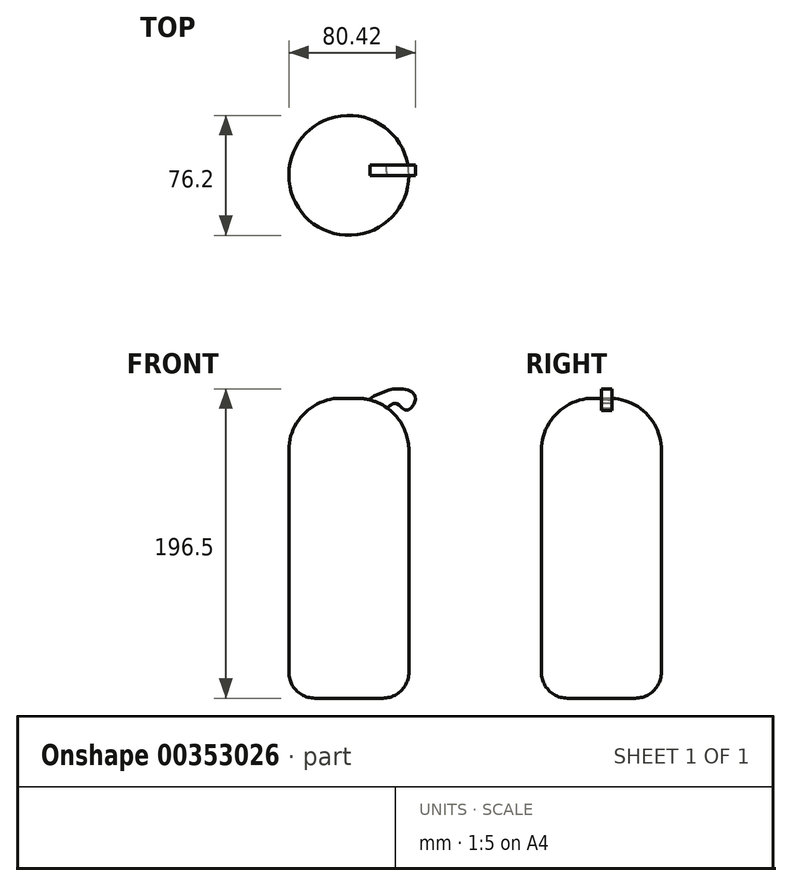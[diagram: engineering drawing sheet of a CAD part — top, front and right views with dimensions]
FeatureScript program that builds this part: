
annotation { "Feature Type Name" : "Feature", "Feature Type Description" : "" }
export const myFeature = defineFeature(function(context is Context, id is Id, definition is map)
    precondition{}
    {
        {
            var Q0;
            Q0=qCreatedBy(makeId("Front.planeOp"),FACE);
            var sketch = newSketch(context, id + "F0", { "sketchPlane" : qUnion([Q0])});
            skLineSegment(sketch, "E0.bottom", {"start": v(-0.42, 101.08) * mm, "end": v(9.74, 101.08) * mm});
            skLineSegment(sketch, "E0.top", {"start": v(-16.93, -89.42) * mm, "end": v(26.25, -89.42) * mm});
            skLineSegment(sketch, "E0.left", {"start": v(-33.44, 68.06) * mm, "end": v(-33.44, -72.91) * mm});
            skLineSegment(sketch, "E0.right", {"start": v(42.76, 68.06) * mm, "end": v(42.76, -72.91) * mm});
            skPoint(sketch, "E1.visualSharp", {"position": v(-33.44, 101.08) * mm});
            skArc(sketch, "E1.filletArc", {"start": v(-0.42, 101.08) * mm, "mid": v(-23.77, 91.4) * mm, "end": v(-33.44, 68.06) * mm});
            skPoint(sketch, "E2.visualSharp", {"position": v(42.76, 101.08) * mm});
            skArc(sketch, "E2.filletArc", {"start": v(42.76, 68.06) * mm, "mid": v(33.1, 91.4) * mm, "end": v(9.74, 101.08) * mm});
            skPoint(sketch, "E3.visualSharp", {"position": v(42.76, -89.42) * mm});
            skArc(sketch, "E3.filletArc", {"start": v(26.25, -89.42) * mm, "mid": v(37.93, -84.58) * mm, "end": v(42.76, -72.91) * mm});
            skPoint(sketch, "E4.visualSharp", {"position": v(-33.44, -89.42) * mm});
            skArc(sketch, "E4.filletArc", {"start": v(-33.44, -72.91) * mm, "mid": v(-28.6, -84.58) * mm, "end": v(-16.93, -89.42) * mm});
            skLineSegment(sketch, "E5", {"start": v(4.66, 101.08) * mm, "end": v(4.66, -89.42) * mm});
            skLineSegment(sketch, "E6", {"start": v(-30.48, 15.24) * mm, "end": v(-30.48, 0) * mm});
            skLineSegment(sketch, "E7", {"start": v(-15.24, 15.24) * mm, "end": v(-15.24, 0) * mm});
            skLineSegment(sketch, "E8", {"start": v(0, 15.24) * mm, "end": v(0, 0) * mm});
            skLineSegment(sketch, "E9", {"start": v(15.24, 15.24) * mm, "end": v(15.24, 0) * mm});
            skLineSegment(sketch, "E10", {"start": v(30.48, 15.24) * mm, "end": v(30.48, 0) * mm});
            skLineSegment(sketch, "E11", {"start": v(40.64, 15.24) * mm, "end": v(40.64, 0) * mm});
            skSolve(sketch);
        }
        {
            var Q0;
            Q0=makeQuery(id+"F0.imprint","IMPRINT",FACE,{"disambiguationData":[TD([[makeQuery(id+"F0.imprint","IMPRINT",EDGE,{"derivedFrom":sQuery(id+"F0.wireOp",EDGE,"E0.right")}),-1.0]])]});
            var Q1;
            Q1=sQuery(id+"F0.wireOp",EDGE,"E11");
            var Q2;
            Q2=sQuery(id+"F0.wireOp",EDGE,"E10");
            var Q3;
            Q3=sQuery(id+"F0.wireOp",EDGE,"E9");
            var Q4;
            Q4=sQuery(id+"F0.wireOp",EDGE,"E5");
            revolve(context, id + "F1", {"entities" : qUnion([Q0]), "surfaceEntities" : qUnion([Q1, Q2, Q3]), "axis" : qUnion([Q4]), "revolveType" : RevolveType.FULL});
        }
        {
            var Q0;
            Q0=qCreatedBy(makeId("Right.planeOp"),FACE);
            var sketch = newSketch(context, id + "F2", { "sketchPlane" : qUnion([Q0])});
            skLineSegment(sketch, "E12", {"start": v(37.35, 0) * mm, "end": v(37.35, 25.6) * mm});
            skLineSegment(sketch, "E13", {"start": v(-38.8, 0) * mm, "end": v(-38.8, 25.6) * mm});
            skSolve(sketch);
        }
        {
            var Q0;
            Q0 = qSketchRegion(id + "F2", true);
            var Q1;
            Q1=sQuery(id+"F2.wireOp",EDGE,"E13");
            var Q2;
            Q2=sQuery(id+"F2.wireOp",EDGE,"E12");
            var Q3;
            Q3=makeQuery(id+"F1.opRevolve","SWEPT_FACE",FACE,{"disambiguationData":[OSD([sQuery(id+"F0.wireOp",EDGE,"E2.filletArc")])]});
            revolve(context, id + "F3", {"bodyType" : ToolBodyType.SURFACE, "entities" : qUnion([Q0]), "surfaceEntities" : qUnion([Q1, Q2]), "axis" : qUnion([Q3]), "revolveType" : RevolveType.FULL});
        }
        {
            var Q0;
            Q0=qCreatedBy(makeId("Front.planeOp"),FACE);
            var sketch = newSketch(context, id + "F4", { "sketchPlane" : qUnion([Q0])});
            skFitSpline(sketch, "E14", {"points": [v(18.03, 99.74) * mm, v(23.26, 103.52) * mm, v(34.3, 107) * mm, v(46.8, 102.35) * mm, v(41.57, 93.34) * mm, v(34.3, 98) * mm, v(25.88, 93.92) * mm, v(18.03, 99.74) * mm]});
            skSolve(sketch);
        }
        {
            var Q0;
            Q0 = qSketchRegion(id + "F4", true);
            extrude(context, id + "F5", {"entities" : qUnion([Q0]), "operationType" : NewBodyOperationType.ADD, "oppositeDirection" : true, "depth" : 6.6 * mm});
        }
    });
